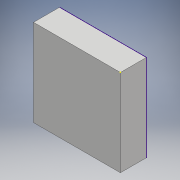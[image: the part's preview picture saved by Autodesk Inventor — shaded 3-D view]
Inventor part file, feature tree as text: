
AUTODESK INVENTOR PART (.ipt)
format: ipt  version: 2018 (Build 220112000, 112)  size: 109,568 bytes
history: native  units: mm
features: sketch x9, extrude x2
ambient origin geometry x8: Origin, YZ Plane, XZ Plane, XY Plane, X Axis, Y Axis, Z Axis, Center Point
bodies: Solid1 (feature_tree)
feature tree (11):
  sketch  "Sketch1"  dims[d0=150.0mm d1=150.0mm]
  extrude  "Extrusion1"  Depth=150.0mm
  extrude  "Extrusion2"  Depth=4.3mm
  sketch  "Sketch4"
  sketch  "Sketch5"
  sketch  "Sketch6"
  sketch  "Sketch7"
  sketch  "Sketch8"
  sketch  "Sketch9"
  sketch  "Sketch2"  dims[d2=10.0mm d3=0.0mm d4=4.3mm]
  sketch  "Sketch3"  dims[d5=35.0mm d6=0.0mm]
